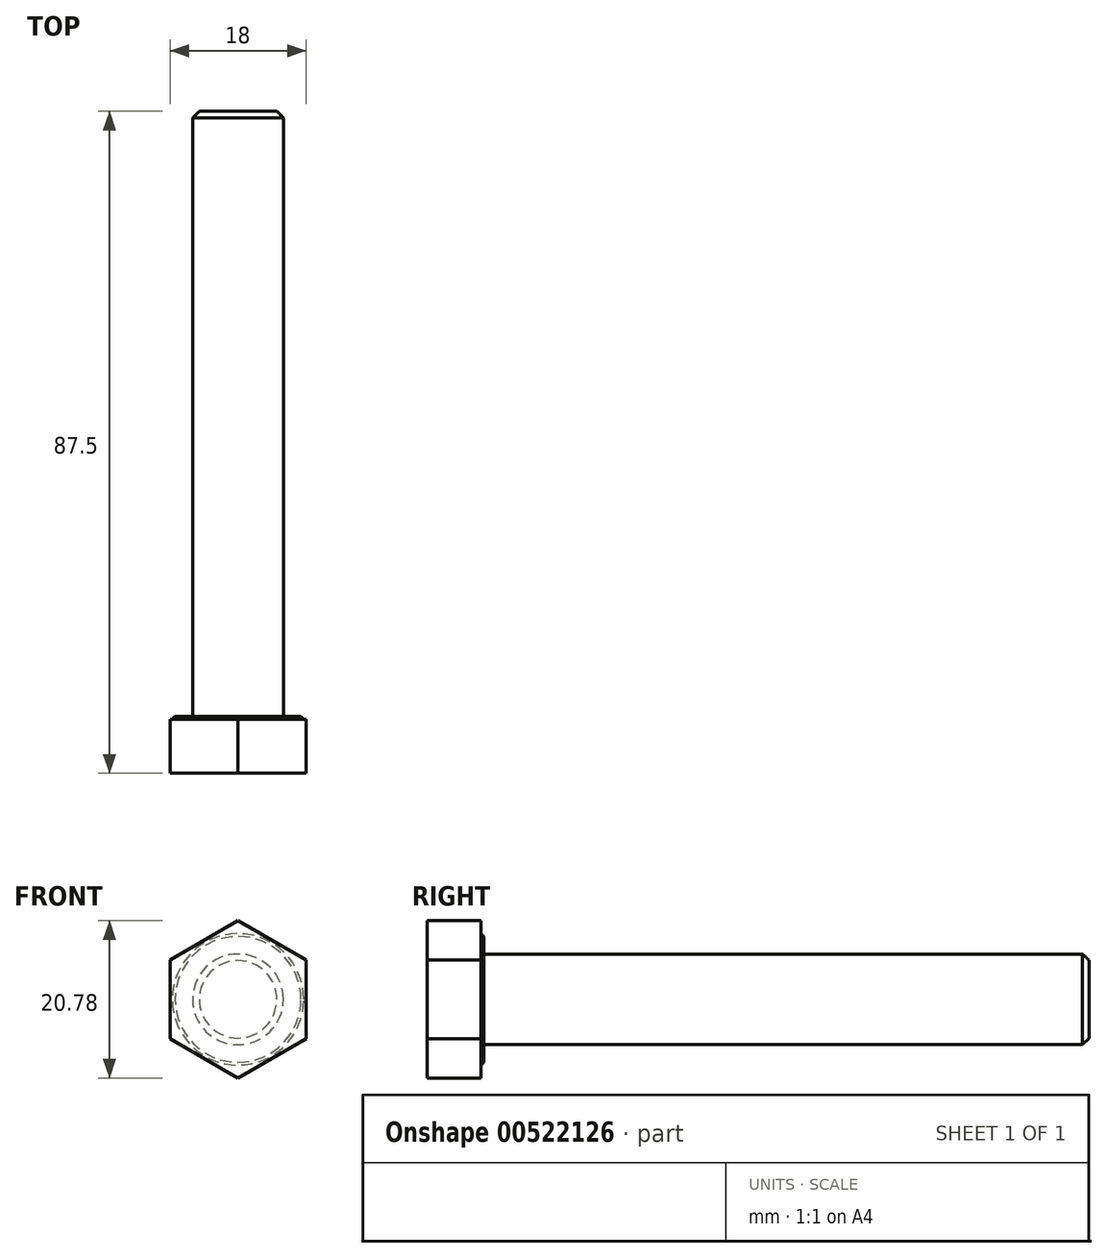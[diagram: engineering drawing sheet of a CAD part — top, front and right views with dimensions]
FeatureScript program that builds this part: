
annotation { "Feature Type Name" : "Feature", "Feature Type Description" : "" }
export const myFeature = defineFeature(function(context is Context, id is Id, definition is map)
    precondition{}
    {
        {
            var Q0;
            Q0=qCreatedBy(makeId("Right.planeOp"),FACE);
            var sketch = newSketch(context, id + "F0", { "sketchPlane" : qUnion([Q0])});
            skLineSegment(sketch, "E0", {"start": v(0, 0) * mm, "end": v(80, 0) * mm});
            skLineSegment(sketch, "E1", {"start": v(80, 0) * mm, "end": v(80, 6) * mm});
            skLineSegment(sketch, "E2", {"start": v(80, 6) * mm, "end": v(0, 6) * mm});
            skLineSegment(sketch, "E3", {"start": v(0, 6) * mm, "end": v(0, 8.32) * mm});
            skLineSegment(sketch, "E4", {"start": v(0, 8.32) * mm, "end": v(-0.37, 8.7) * mm});
            skLineSegment(sketch, "E5", {"start": v(-0.38, 8.7) * mm, "end": v(-0.38, 9) * mm});
            skLineSegment(sketch, "E6", {"start": v(-0.38, 9) * mm, "end": v(-7.5, 9) * mm});
            skLineSegment(sketch, "E7", {"start": v(-7.5, 9) * mm, "end": v(-7.5, 0) * mm});
            skLineSegment(sketch, "E8", {"start": v(-7.5, 0) * mm, "end": v(0, 0) * mm});
            skLineSegment(sketch, "E9", {"start": v(-7.5, 0) * mm, "end": v(-20.78, 0) * mm, "construction": true});
            skSolve(sketch);
        }
        {
            var Q0;
            Q0=makeQuery(id+"F0.imprint","IMPRINT",FACE,{"disambiguationData":[TD([[makeQuery(id+"F0.imprint","IMPRINT",EDGE,{"derivedFrom":sQuery(id+"F0.wireOp",EDGE,"E0")}),1.0]])]});
            var Q1;
            Q1=sQuery(id+"F0.wireOp",EDGE,"E9");
            revolve(context, id + "F1", {"entities" : qUnion([Q0]), "axis" : qUnion([Q1]), "revolveType" : RevolveType.FULL});
        }
        {
            var Q0;
            Q0=makeQuery(id+"F1.opRevolve","SWEPT_FACE",FACE,{"disambiguationData":[OSD([sQuery(id+"F0.wireOp",EDGE,"E7")])]});
            var sketch = newSketch(context, id + "F2", { "sketchPlane" : qUnion([Q0])});
            skCircle(sketch, "E10.cCircle", {"center": v(0, 0) * mm, "radius": 9 * mm, "construction": true});
            skLineSegment(sketch, "E10.0", {"start": v(9, 5.2) * mm, "end": v(9, -5.2) * mm});
            skLineSegment(sketch, "E10.1", {"start": v(9, -5.2) * mm, "end": v(0, -10.4) * mm});
            skLineSegment(sketch, "E10.2", {"start": v(0, -10.4) * mm, "end": v(-9, -5.2) * mm});
            skLineSegment(sketch, "E10.3", {"start": v(-9, -5.2) * mm, "end": v(-9, 5.2) * mm});
            skLineSegment(sketch, "E10.4", {"start": v(-9, 5.2) * mm, "end": v(0, 10.4) * mm});
            skLineSegment(sketch, "E10.5", {"start": v(0, 10.4) * mm, "end": v(9, 5.2) * mm});
            skPoint(sketch, "E10.0.midPoint", {"position": v(9, 0) * mm});
            skSolve(sketch);
        }
        {
            var Q0;
            Q0 = qSketchRegion(id + "F2", true);
            var Q1;
            Q1=makeQuery(id+"F1.opRevolve","SWEPT_FACE",FACE,{"disambiguationData":[OSD([sQuery(id+"F0.wireOp",EDGE,"E5")])]});
            extrude(context, id + "F3", {"entities" : qUnion([Q0]), "operationType" : NewBodyOperationType.ADD, "endBound" : BoundingType.UP_TO_SURFACE, "oppositeDirection" : true, "depth" : 25 * mm, "endBoundEntityFace" : qUnion([Q1]), "offsetDistance" : 25 * mm});
        }
        {
            var Q0;
            Q0=makeQuery(id+"F1.opRevolve","SWEPT_EDGE",EDGE,{"disambiguationData":[OSD([sQuery(id+"F0.wireOp",EDGE,"E1"),sQuery(id+"F0.wireOp",EDGE,"E2")])]});
            chamfer(context, id + "F4", {"entities" : qUnion([Q0]), "width" : (1.75 / 2) * mm, "tangentPropagation" : true});
        }
    });
